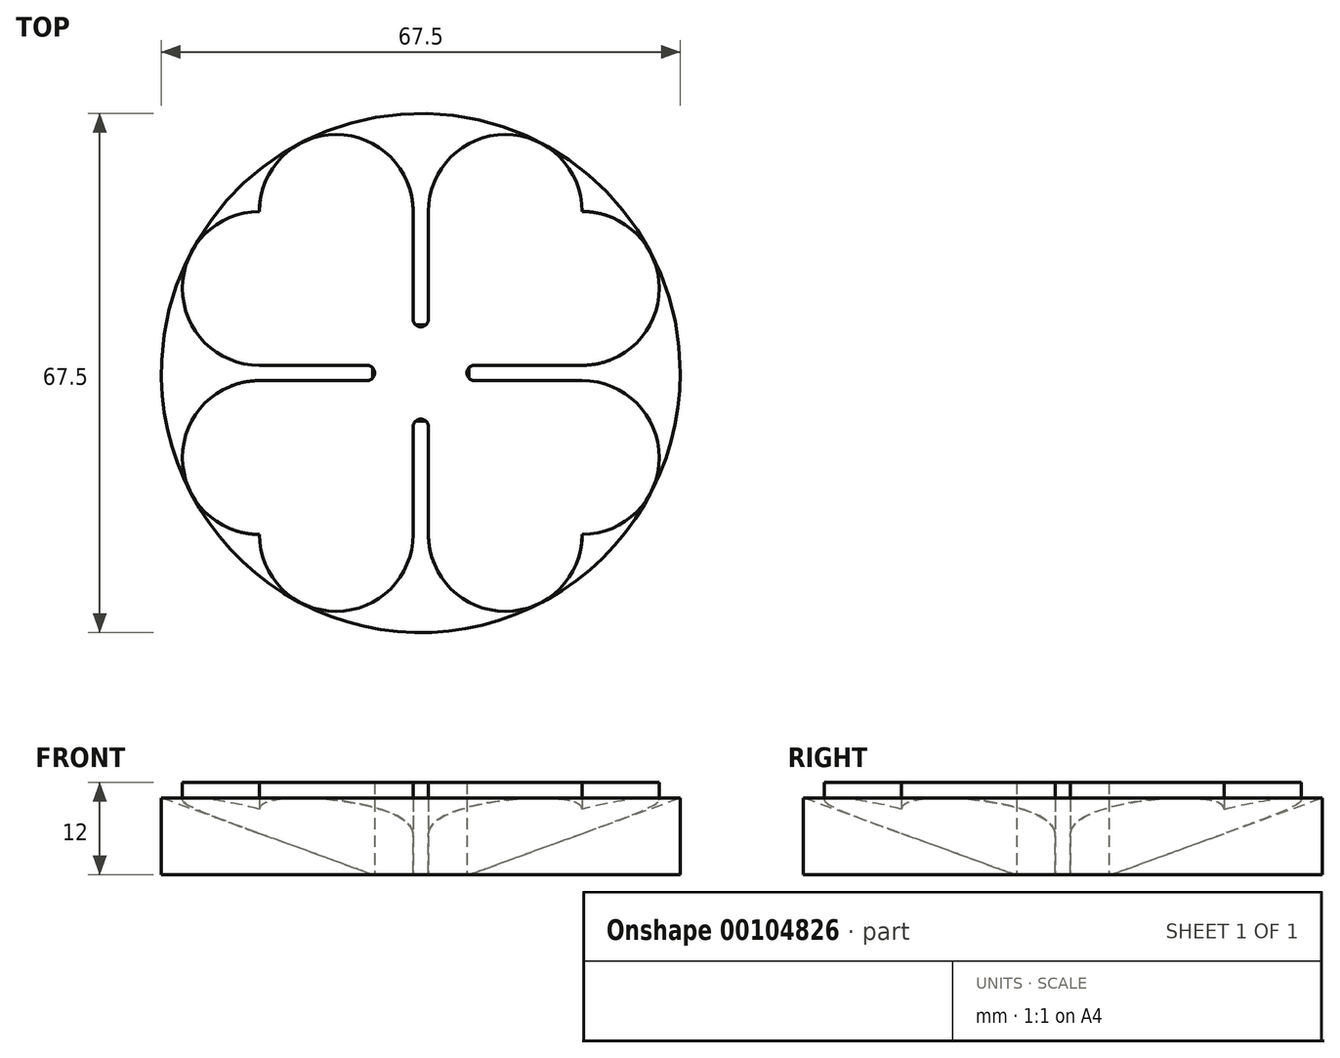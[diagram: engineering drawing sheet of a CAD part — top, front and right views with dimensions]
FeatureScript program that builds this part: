
annotation { "Feature Type Name" : "Feature", "Feature Type Description" : "" }
export const myFeature = defineFeature(function(context is Context, id is Id, definition is map)
    precondition{}
    {
        {
            var Q0;
            Q0=qCreatedBy(makeId("Top.planeOp"),FACE);
            var sketch = newSketch(context, id + "F0", { "sketchPlane" : qUnion([Q0])});
            skPoint(sketch, "E0.middle", {"position": v(0, 0) * mm});
            skLineSegment(sketch, "E1", {"start": v(0, 0) * mm, "end": v(-21, 0) * mm});
            skLineSegment(sketch, "E2", {"start": v(-21, 0) * mm, "end": v(-21, 11) * mm});
            skLineSegment(sketch, "E3", {"start": v(-21, 0) * mm, "end": v(-21, -11) * mm});
            skLineSegment(sketch, "E4", {"start": v(0, 0) * mm, "end": v(21, 0) * mm});
            skLineSegment(sketch, "E5", {"start": v(21, 0) * mm, "end": v(21, 11) * mm});
            skLineSegment(sketch, "E6", {"start": v(21, 0) * mm, "end": v(21, -11) * mm});
            skLineSegment(sketch, "E7", {"start": v(0, 0) * mm, "end": v(0, -21) * mm});
            skLineSegment(sketch, "E8", {"start": v(0, -21) * mm, "end": v(-11, -21) * mm});
            skLineSegment(sketch, "E9", {"start": v(0, -21) * mm, "end": v(11, -21) * mm});
            skCircle(sketch, "E10", {"center": v(11, -21) * mm, "radius": 10 * mm});
            skCircle(sketch, "E11", {"center": v(21, -11) * mm, "radius": 10 * mm});
            skCircle(sketch, "E12", {"center": v(21, 11) * mm, "radius": 10 * mm});
            skCircle(sketch, "E13", {"center": v(-21, 11) * mm, "radius": 10 * mm});
            skCircle(sketch, "E14", {"center": v(-21, -11) * mm, "radius": 10 * mm});
            skCircle(sketch, "E15", {"center": v(-11, -21) * mm, "radius": 10 * mm});
            skLineSegment(sketch, "E16", {"start": v(0, 0) * mm, "end": v(7, 0) * mm});
            skLineSegment(sketch, "E17", {"start": v(0, 0) * mm, "end": v(-7, 0) * mm});
            skLineSegment(sketch, "E18", {"start": v(0, 0) * mm, "end": v(0, -7) * mm});
            skCircle(sketch, "E19", {"center": v(7, 0) * mm, "radius": 1 * mm});
            skCircle(sketch, "E20", {"center": v(-7, 0) * mm, "radius": 1 * mm});
            skCircle(sketch, "E21", {"center": v(0, -7) * mm, "radius": 1 * mm});
            skLineSegment(sketch, "E22", {"start": v(0, 0) * mm, "end": v(0, 21) * mm});
            skLineSegment(sketch, "E23", {"start": v(0, 21) * mm, "end": v(11, 21) * mm});
            skLineSegment(sketch, "E24", {"start": v(0, 21) * mm, "end": v(-11, 21) * mm});
            skLineSegment(sketch, "E25", {"start": v(0, 0) * mm, "end": v(0, 7) * mm});
            skCircle(sketch, "E26", {"center": v(0, 7) * mm, "radius": 1 * mm});
            skCircle(sketch, "E27", {"center": v(-11, 21) * mm, "radius": 10 * mm});
            skCircle(sketch, "E28", {"center": v(11, 21) * mm, "radius": 10 * mm});
            skLineSegment(sketch, "E29", {"start": v(-1, 7) * mm, "end": v(-1, 21) * mm});
            skPoint(sketch, "E29.endSnap0", {"position": v(-5.5, 21) * mm});
            skLineSegment(sketch, "E30", {"start": v(7, 1) * mm, "end": v(21, 1) * mm});
            skLineSegment(sketch, "E31", {"start": v(7, -1) * mm, "end": v(21, -1) * mm});
            skLineSegment(sketch, "E32", {"start": v(1, -7) * mm, "end": v(1, -21) * mm});
            skLineSegment(sketch, "E33", {"start": v(-1, -7) * mm, "end": v(-1, -21) * mm});
            skLineSegment(sketch, "E34", {"start": v(-7, 1) * mm, "end": v(-21, 1) * mm});
            skLineSegment(sketch, "E35", {"start": v(-7, -1) * mm, "end": v(-21, -1) * mm});
            skCircle(sketch, "E36", {"center": v(0, 0) * mm, "radius": 33.75 * mm});
            skLineSegment(sketch, "E37", {"start": v(1, 7) * mm, "end": v(1, 21) * mm});
            skSolve(sketch);
        }
        {
            var Q0;
            {var subQ0=sQuery(id+"F0.wireOp",EDGE,"E13");var subQ2=sQuery(id+"F0.wireOp",EDGE,"E27");var subQ3=makeQuery(id+"F0.imprint","INTERSECT",VERTEX,{"disambiguationData":[OD(0.0)],"derivedFrom":[subQ0,subQ2]});Q0=makeQuery(id+"F0.imprint","IMPRINT",FACE,{"disambiguationData":[TD([[makeQuery(id+"F0.imprint","IMPRINT",EDGE,{"disambiguationData":[TD([[subQ3,-1.0]])],"derivedFrom":subQ2}),-1.0]])]});}
            var Q1;
            {var subQ0=sQuery(id+"F0.wireOp",EDGE,"E27");var subQ1=sQuery(id+"F0.wireOp",EDGE,"E13");var subQ2=makeQuery(id+"F0.imprint","INTERSECT",VERTEX,{"disambiguationData":[OD(0.0)],"derivedFrom":[subQ1,subQ0]});Q1=makeQuery(id+"F0.imprint","IMPRINT",FACE,{"disambiguationData":[TD([[makeQuery(id+"F0.imprint","IMPRINT",EDGE,{"disambiguationData":[TD([[subQ2,1.0]])],"derivedFrom":subQ1}),1.0]])]});}
            var Q2;
            {var subQ0=sQuery(id+"F0.wireOp",EDGE,"E27");var subQ1=sQuery(id+"F0.wireOp",EDGE,"E13");var subQ2=makeQuery(id+"F0.imprint","INTERSECT",VERTEX,{"disambiguationData":[OD(0.0)],"derivedFrom":[subQ1,subQ0]});Q2=makeQuery(id+"F0.imprint","IMPRINT",FACE,{"disambiguationData":[TD([[makeQuery(id+"F0.imprint","IMPRINT",EDGE,{"disambiguationData":[TD([[subQ2,1.0]])],"derivedFrom":subQ1}),-1.0]])]});}
            var Q3;
            {var subQ0=sQuery(id+"F0.wireOp",EDGE,"E28");var subQ1=sQuery(id+"F0.wireOp",EDGE,"E12");var subQ2=makeQuery(id+"F0.imprint","INTERSECT",VERTEX,{"disambiguationData":[OD(0.0)],"derivedFrom":[subQ1,subQ0]});Q3=makeQuery(id+"F0.imprint","IMPRINT",FACE,{"disambiguationData":[TD([[makeQuery(id+"F0.imprint","IMPRINT",EDGE,{"disambiguationData":[TD([[subQ2,1.0]])],"derivedFrom":subQ1}),-1.0]])]});}
            var Q4;
            {var subQ0=sQuery(id+"F0.wireOp",EDGE,"E28");var subQ1=sQuery(id+"F0.wireOp",EDGE,"E12");var subQ2=makeQuery(id+"F0.imprint","INTERSECT",VERTEX,{"disambiguationData":[OD(0.0)],"derivedFrom":[subQ1,subQ0]});Q4=makeQuery(id+"F0.imprint","IMPRINT",FACE,{"disambiguationData":[TD([[makeQuery(id+"F0.imprint","IMPRINT",EDGE,{"disambiguationData":[TD([[subQ2,1.0]])],"derivedFrom":subQ1}),1.0]])]});}
            var Q5;
            {var subQ0=sQuery(id+"F0.wireOp",EDGE,"E12");var subQ2=sQuery(id+"F0.wireOp",EDGE,"E28");var subQ3=makeQuery(id+"F0.imprint","INTERSECT",VERTEX,{"disambiguationData":[OD(0.0)],"derivedFrom":[subQ0,subQ2]});Q5=makeQuery(id+"F0.imprint","IMPRINT",FACE,{"disambiguationData":[TD([[makeQuery(id+"F0.imprint","IMPRINT",EDGE,{"disambiguationData":[TD([[subQ3,-1.0]])],"derivedFrom":subQ2}),-1.0]])]});}
            var Q6;
            {var subQ0=sQuery(id+"F0.wireOp",EDGE,"E11");var subQ1=sQuery(id+"F0.wireOp",EDGE,"E10");var subQ2=makeQuery(id+"F0.imprint","INTERSECT",VERTEX,{"disambiguationData":[OD(0.0)],"derivedFrom":[subQ1,subQ0]});Q6=makeQuery(id+"F0.imprint","IMPRINT",FACE,{"disambiguationData":[TD([[makeQuery(id+"F0.imprint","IMPRINT",EDGE,{"disambiguationData":[TD([[subQ2,1.0]])],"derivedFrom":subQ1}),-1.0]])]});}
            var Q7;
            {var subQ0=sQuery(id+"F0.wireOp",EDGE,"E11");var subQ1=sQuery(id+"F0.wireOp",EDGE,"E10");var subQ2=makeQuery(id+"F0.imprint","INTERSECT",VERTEX,{"disambiguationData":[OD(0.0)],"derivedFrom":[subQ1,subQ0]});Q7=makeQuery(id+"F0.imprint","IMPRINT",FACE,{"disambiguationData":[TD([[makeQuery(id+"F0.imprint","IMPRINT",EDGE,{"disambiguationData":[TD([[subQ2,1.0]])],"derivedFrom":subQ1}),1.0]])]});}
            var Q8;
            {var subQ0=sQuery(id+"F0.wireOp",EDGE,"E10");var subQ2=sQuery(id+"F0.wireOp",EDGE,"E11");var subQ3=makeQuery(id+"F0.imprint","INTERSECT",VERTEX,{"disambiguationData":[OD(0.0)],"derivedFrom":[subQ0,subQ2]});Q8=makeQuery(id+"F0.imprint","IMPRINT",FACE,{"disambiguationData":[TD([[makeQuery(id+"F0.imprint","IMPRINT",EDGE,{"disambiguationData":[TD([[subQ3,-1.0]])],"derivedFrom":subQ2}),-1.0]])]});}
            var Q9;
            {var subQ0=sQuery(id+"F0.wireOp",EDGE,"E15");var subQ1=sQuery(id+"F0.wireOp",EDGE,"E14");var subQ2=makeQuery(id+"F0.imprint","INTERSECT",VERTEX,{"disambiguationData":[OD(0.0)],"derivedFrom":[subQ1,subQ0]});Q9=makeQuery(id+"F0.imprint","IMPRINT",FACE,{"disambiguationData":[TD([[makeQuery(id+"F0.imprint","IMPRINT",EDGE,{"disambiguationData":[TD([[subQ2,1.0]])],"derivedFrom":subQ1}),-1.0]])]});}
            var Q10;
            {var subQ0=sQuery(id+"F0.wireOp",EDGE,"E15");var subQ1=sQuery(id+"F0.wireOp",EDGE,"E14");var subQ2=makeQuery(id+"F0.imprint","INTERSECT",VERTEX,{"disambiguationData":[OD(0.0)],"derivedFrom":[subQ1,subQ0]});Q10=makeQuery(id+"F0.imprint","IMPRINT",FACE,{"disambiguationData":[TD([[makeQuery(id+"F0.imprint","IMPRINT",EDGE,{"disambiguationData":[TD([[subQ2,1.0]])],"derivedFrom":subQ1}),1.0]])]});}
            var Q11;
            {var subQ0=sQuery(id+"F0.wireOp",EDGE,"E14");var subQ2=sQuery(id+"F0.wireOp",EDGE,"E15");var subQ3=makeQuery(id+"F0.imprint","INTERSECT",VERTEX,{"disambiguationData":[OD(0.0)],"derivedFrom":[subQ0,subQ2]});Q11=makeQuery(id+"F0.imprint","IMPRINT",FACE,{"disambiguationData":[TD([[makeQuery(id+"F0.imprint","IMPRINT",EDGE,{"disambiguationData":[TD([[subQ3,-1.0]])],"derivedFrom":subQ2}),-1.0]])]});}
            var Q12;
            {var subQ7=sQuery(id+"F0.wireOp",EDGE,"E33");Q12=makeQuery(id+"F0.imprint","IMPRINT",FACE,{"disambiguationData":[TD([[makeQuery(id+"F0.imprint","IMPRINT",EDGE,{"derivedFrom":subQ7}),-1.0]])]});}
            var Q13;
            {var subQ7=sQuery(id+"F0.wireOp",EDGE,"E31");Q13=makeQuery(id+"F0.imprint","IMPRINT",FACE,{"disambiguationData":[TD([[makeQuery(id+"F0.imprint","IMPRINT",EDGE,{"derivedFrom":subQ7}),-1.0]])]});}
            var Q14;
            {var subQ7=sQuery(id+"F0.wireOp",EDGE,"E30");Q14=makeQuery(id+"F0.imprint","IMPRINT",FACE,{"disambiguationData":[TD([[makeQuery(id+"F0.imprint","IMPRINT",EDGE,{"derivedFrom":subQ7}),1.0]])]});}
            var Q15;
            {var subQ11=sQuery(id+"F0.wireOp",EDGE,"E29");Q15=makeQuery(id+"F0.imprint","IMPRINT",FACE,{"disambiguationData":[TD([[makeQuery(id+"F0.imprint","IMPRINT",EDGE,{"derivedFrom":subQ11}),1.0]])]});}
            var Q16;
            Q16=makeQuery(id+"F0.imprint","IMPRINT",FACE,{"disambiguationData":[TD([[makeQuery(id+"F0.imprint","IMPRINT",EDGE,{"derivedFrom":sQuery(id+"F0.wireOp",EDGE,"E36")}),1.0]])]});
            var Q17;
            {var subQ5=sQuery(id+"F0.wireOp",EDGE,"E37");Q17=makeQuery(id+"F0.imprint","IMPRINT",FACE,{"disambiguationData":[TD([[makeQuery(id+"F0.imprint","IMPRINT",EDGE,{"derivedFrom":subQ5}),1.0]])]});}
            var Q18;
            {var subQ5=sQuery(id+"F0.wireOp",EDGE,"E29");Q18=makeQuery(id+"F0.imprint","IMPRINT",FACE,{"disambiguationData":[TD([[makeQuery(id+"F0.imprint","IMPRINT",EDGE,{"derivedFrom":subQ5}),-1.0]])]});}
            var Q19;
            {var subQ0=sQuery(id+"F0.wireOp",EDGE,"E25");var subQ1=sQuery(id+"F0.wireOp",EDGE,"E22");var subQ2=makeQuery(id+"F0.imprint","INTERSECT",VERTEX,{"derivedFrom":[subQ1,subQ0]});Q19=makeQuery(id+"F0.imprint","IMPRINT",FACE,{"disambiguationData":[TD([[makeQuery(id+"F0.imprint","IMPRINT",EDGE,{"disambiguationData":[TD([[subQ2,-1.0]])],"derivedFrom":subQ1}),1.0]])]});}
            var Q20;
            {var subQ0=sQuery(id+"F0.wireOp",EDGE,"E25");var subQ1=sQuery(id+"F0.wireOp",EDGE,"E22");var subQ2=makeQuery(id+"F0.imprint","INTERSECT",VERTEX,{"derivedFrom":[subQ1,subQ0]});Q20=makeQuery(id+"F0.imprint","IMPRINT",FACE,{"disambiguationData":[TD([[makeQuery(id+"F0.imprint","IMPRINT",EDGE,{"disambiguationData":[TD([[subQ2,-1.0]])],"derivedFrom":subQ1}),-1.0]])]});}
            var Q21;
            {var subQ5=sQuery(id+"F0.wireOp",EDGE,"E35");Q21=makeQuery(id+"F0.imprint","IMPRINT",FACE,{"disambiguationData":[TD([[makeQuery(id+"F0.imprint","IMPRINT",EDGE,{"derivedFrom":subQ5}),-1.0]])]});}
            var Q22;
            {var subQ5=sQuery(id+"F0.wireOp",EDGE,"E34");Q22=makeQuery(id+"F0.imprint","IMPRINT",FACE,{"disambiguationData":[TD([[makeQuery(id+"F0.imprint","IMPRINT",EDGE,{"derivedFrom":subQ5}),1.0]])]});}
            var Q23;
            {var subQ0=sQuery(id+"F0.wireOp",EDGE,"E17");var subQ1=sQuery(id+"F0.wireOp",EDGE,"E1");var subQ2=makeQuery(id+"F0.imprint","INTERSECT",VERTEX,{"derivedFrom":[subQ1,subQ0]});Q23=makeQuery(id+"F0.imprint","IMPRINT",FACE,{"disambiguationData":[TD([[makeQuery(id+"F0.imprint","IMPRINT",EDGE,{"disambiguationData":[TD([[subQ2,-1.0]])],"derivedFrom":subQ1}),-1.0]])]});}
            var Q24;
            {var subQ0=sQuery(id+"F0.wireOp",EDGE,"E17");var subQ1=sQuery(id+"F0.wireOp",EDGE,"E1");var subQ2=makeQuery(id+"F0.imprint","INTERSECT",VERTEX,{"derivedFrom":[subQ1,subQ0]});Q24=makeQuery(id+"F0.imprint","IMPRINT",FACE,{"disambiguationData":[TD([[makeQuery(id+"F0.imprint","IMPRINT",EDGE,{"disambiguationData":[TD([[subQ2,-1.0]])],"derivedFrom":subQ1}),1.0]])]});}
            var Q25;
            {var subQ0=sQuery(id+"F0.wireOp",EDGE,"E16");var subQ1=sQuery(id+"F0.wireOp",EDGE,"E4");var subQ2=makeQuery(id+"F0.imprint","INTERSECT",VERTEX,{"derivedFrom":[subQ1,subQ0]});Q25=makeQuery(id+"F0.imprint","IMPRINT",FACE,{"disambiguationData":[TD([[makeQuery(id+"F0.imprint","IMPRINT",EDGE,{"disambiguationData":[TD([[subQ2,-1.0]])],"derivedFrom":subQ1}),-1.0]])]});}
            var Q26;
            {var subQ0=sQuery(id+"F0.wireOp",EDGE,"E16");var subQ1=sQuery(id+"F0.wireOp",EDGE,"E4");var subQ2=makeQuery(id+"F0.imprint","INTERSECT",VERTEX,{"derivedFrom":[subQ1,subQ0]});Q26=makeQuery(id+"F0.imprint","IMPRINT",FACE,{"disambiguationData":[TD([[makeQuery(id+"F0.imprint","IMPRINT",EDGE,{"disambiguationData":[TD([[subQ2,-1.0]])],"derivedFrom":subQ1}),1.0]])]});}
            var Q27;
            {var subQ5=sQuery(id+"F0.wireOp",EDGE,"E30");Q27=makeQuery(id+"F0.imprint","IMPRINT",FACE,{"disambiguationData":[TD([[makeQuery(id+"F0.imprint","IMPRINT",EDGE,{"derivedFrom":subQ5}),-1.0]])]});}
            var Q28;
            {var subQ5=sQuery(id+"F0.wireOp",EDGE,"E31");Q28=makeQuery(id+"F0.imprint","IMPRINT",FACE,{"disambiguationData":[TD([[makeQuery(id+"F0.imprint","IMPRINT",EDGE,{"derivedFrom":subQ5}),1.0]])]});}
            var Q29;
            {var subQ5=sQuery(id+"F0.wireOp",EDGE,"E32");Q29=makeQuery(id+"F0.imprint","IMPRINT",FACE,{"disambiguationData":[TD([[makeQuery(id+"F0.imprint","IMPRINT",EDGE,{"derivedFrom":subQ5}),-1.0]])]});}
            var Q30;
            {var subQ5=sQuery(id+"F0.wireOp",EDGE,"E33");Q30=makeQuery(id+"F0.imprint","IMPRINT",FACE,{"disambiguationData":[TD([[makeQuery(id+"F0.imprint","IMPRINT",EDGE,{"derivedFrom":subQ5}),1.0]])]});}
            var Q31;
            {var subQ0=sQuery(id+"F0.wireOp",EDGE,"E18");var subQ1=sQuery(id+"F0.wireOp",EDGE,"E7");var subQ2=makeQuery(id+"F0.imprint","INTERSECT",VERTEX,{"derivedFrom":[subQ1,subQ0]});Q31=makeQuery(id+"F0.imprint","IMPRINT",FACE,{"disambiguationData":[TD([[makeQuery(id+"F0.imprint","IMPRINT",EDGE,{"disambiguationData":[TD([[subQ2,-1.0]])],"derivedFrom":subQ1}),-1.0]])]});}
            var Q32;
            {var subQ0=sQuery(id+"F0.wireOp",EDGE,"E18");var subQ1=sQuery(id+"F0.wireOp",EDGE,"E7");var subQ2=makeQuery(id+"F0.imprint","INTERSECT",VERTEX,{"derivedFrom":[subQ1,subQ0]});Q32=makeQuery(id+"F0.imprint","IMPRINT",FACE,{"disambiguationData":[TD([[makeQuery(id+"F0.imprint","IMPRINT",EDGE,{"disambiguationData":[TD([[subQ2,-1.0]])],"derivedFrom":subQ1}),1.0]])]});}
            extrude(context, id + "F1", {"entities" : qUnion([Q0, Q1, Q2, Q3, Q4, Q5, Q6, Q7, Q8, Q9, Q10, Q11, Q12, Q13, Q14, Q15, Q16, Q17, Q18, Q19, Q20, Q21, Q22, Q23, Q24, Q25, Q26, Q27, Q28, Q29, Q30, Q31, Q32]), "depth" : 10 * mm});
        }
        {
            var Q0;
            Q0=makeQuery(id+"F1.opExtrude","CAP_FACE",FACE,{"disambiguationData":[OSD([sQuery(id+"F0.wireOp",EDGE,"E36")])],"isStart":false});
            var sketch = newSketch(context, id + "F2", { "sketchPlane" : qUnion([Q0])});
            skCircle(sketch, "E38", {"center": v(0, 0) * mm, "radius": 33.75 * mm});
            skSolve(sketch);
        }
        {
            var Q0;
            Q0 = qSketchRegion(id + "F2", true);
            extrude(context, id + "F3", {"entities" : qUnion([Q0]), "operationType" : NewBodyOperationType.REMOVE, "oppositeDirection" : true, "depth" : 10 * mm, "hasDraft" : true, "draftAngle" : 70 * degree, "draftPullDirection" : true});
        }
        {
            var Q0;
            {var subQ0=sQuery(id+"F0.wireOp",EDGE,"E10");var subQ2=sQuery(id+"F0.wireOp",EDGE,"E11");var subQ3=makeQuery(id+"F0.imprint","INTERSECT",VERTEX,{"disambiguationData":[OD(0.0)],"derivedFrom":[subQ0,subQ2]});Q0=makeQuery(id+"F0.imprint","IMPRINT",FACE,{"disambiguationData":[TD([[makeQuery(id+"F0.imprint","IMPRINT",EDGE,{"disambiguationData":[TD([[subQ3,-1.0]])],"derivedFrom":subQ2}),-1.0]])]});}
            var Q1;
            {var subQ0=sQuery(id+"F0.wireOp",EDGE,"E11");var subQ1=sQuery(id+"F0.wireOp",EDGE,"E10");var subQ2=makeQuery(id+"F0.imprint","INTERSECT",VERTEX,{"disambiguationData":[OD(0.0)],"derivedFrom":[subQ1,subQ0]});Q1=makeQuery(id+"F0.imprint","IMPRINT",FACE,{"disambiguationData":[TD([[makeQuery(id+"F0.imprint","IMPRINT",EDGE,{"disambiguationData":[TD([[subQ2,1.0]])],"derivedFrom":subQ1}),1.0]])]});}
            var Q2;
            {var subQ0=sQuery(id+"F0.wireOp",EDGE,"E11");var subQ1=sQuery(id+"F0.wireOp",EDGE,"E10");var subQ2=makeQuery(id+"F0.imprint","INTERSECT",VERTEX,{"disambiguationData":[OD(0.0)],"derivedFrom":[subQ1,subQ0]});Q2=makeQuery(id+"F0.imprint","IMPRINT",FACE,{"disambiguationData":[TD([[makeQuery(id+"F0.imprint","IMPRINT",EDGE,{"disambiguationData":[TD([[subQ2,1.0]])],"derivedFrom":subQ1}),-1.0]])]});}
            var Q3;
            {var subQ0=sQuery(id+"F0.wireOp",EDGE,"E12");var subQ2=sQuery(id+"F0.wireOp",EDGE,"E28");var subQ3=makeQuery(id+"F0.imprint","INTERSECT",VERTEX,{"disambiguationData":[OD(0.0)],"derivedFrom":[subQ0,subQ2]});Q3=makeQuery(id+"F0.imprint","IMPRINT",FACE,{"disambiguationData":[TD([[makeQuery(id+"F0.imprint","IMPRINT",EDGE,{"disambiguationData":[TD([[subQ3,-1.0]])],"derivedFrom":subQ2}),-1.0]])]});}
            var Q4;
            {var subQ0=sQuery(id+"F0.wireOp",EDGE,"E28");var subQ1=sQuery(id+"F0.wireOp",EDGE,"E12");var subQ2=makeQuery(id+"F0.imprint","INTERSECT",VERTEX,{"disambiguationData":[OD(0.0)],"derivedFrom":[subQ1,subQ0]});Q4=makeQuery(id+"F0.imprint","IMPRINT",FACE,{"disambiguationData":[TD([[makeQuery(id+"F0.imprint","IMPRINT",EDGE,{"disambiguationData":[TD([[subQ2,1.0]])],"derivedFrom":subQ1}),1.0]])]});}
            var Q5;
            {var subQ0=sQuery(id+"F0.wireOp",EDGE,"E28");var subQ1=sQuery(id+"F0.wireOp",EDGE,"E12");var subQ2=makeQuery(id+"F0.imprint","INTERSECT",VERTEX,{"disambiguationData":[OD(0.0)],"derivedFrom":[subQ1,subQ0]});Q5=makeQuery(id+"F0.imprint","IMPRINT",FACE,{"disambiguationData":[TD([[makeQuery(id+"F0.imprint","IMPRINT",EDGE,{"disambiguationData":[TD([[subQ2,1.0]])],"derivedFrom":subQ1}),-1.0]])]});}
            var Q6;
            {var subQ0=sQuery(id+"F0.wireOp",EDGE,"E27");var subQ1=sQuery(id+"F0.wireOp",EDGE,"E13");var subQ2=makeQuery(id+"F0.imprint","INTERSECT",VERTEX,{"disambiguationData":[OD(0.0)],"derivedFrom":[subQ1,subQ0]});Q6=makeQuery(id+"F0.imprint","IMPRINT",FACE,{"disambiguationData":[TD([[makeQuery(id+"F0.imprint","IMPRINT",EDGE,{"disambiguationData":[TD([[subQ2,1.0]])],"derivedFrom":subQ1}),-1.0]])]});}
            var Q7;
            {var subQ0=sQuery(id+"F0.wireOp",EDGE,"E27");var subQ1=sQuery(id+"F0.wireOp",EDGE,"E13");var subQ2=makeQuery(id+"F0.imprint","INTERSECT",VERTEX,{"disambiguationData":[OD(0.0)],"derivedFrom":[subQ1,subQ0]});Q7=makeQuery(id+"F0.imprint","IMPRINT",FACE,{"disambiguationData":[TD([[makeQuery(id+"F0.imprint","IMPRINT",EDGE,{"disambiguationData":[TD([[subQ2,1.0]])],"derivedFrom":subQ1}),1.0]])]});}
            var Q8;
            {var subQ0=sQuery(id+"F0.wireOp",EDGE,"E13");var subQ2=sQuery(id+"F0.wireOp",EDGE,"E27");var subQ3=makeQuery(id+"F0.imprint","INTERSECT",VERTEX,{"disambiguationData":[OD(0.0)],"derivedFrom":[subQ0,subQ2]});Q8=makeQuery(id+"F0.imprint","IMPRINT",FACE,{"disambiguationData":[TD([[makeQuery(id+"F0.imprint","IMPRINT",EDGE,{"disambiguationData":[TD([[subQ3,-1.0]])],"derivedFrom":subQ2}),-1.0]])]});}
            var Q9;
            {var subQ0=sQuery(id+"F0.wireOp",EDGE,"E14");var subQ2=sQuery(id+"F0.wireOp",EDGE,"E15");var subQ3=makeQuery(id+"F0.imprint","INTERSECT",VERTEX,{"disambiguationData":[OD(0.0)],"derivedFrom":[subQ0,subQ2]});Q9=makeQuery(id+"F0.imprint","IMPRINT",FACE,{"disambiguationData":[TD([[makeQuery(id+"F0.imprint","IMPRINT",EDGE,{"disambiguationData":[TD([[subQ3,-1.0]])],"derivedFrom":subQ2}),-1.0]])]});}
            var Q10;
            {var subQ0=sQuery(id+"F0.wireOp",EDGE,"E15");var subQ1=sQuery(id+"F0.wireOp",EDGE,"E14");var subQ2=makeQuery(id+"F0.imprint","INTERSECT",VERTEX,{"disambiguationData":[OD(0.0)],"derivedFrom":[subQ1,subQ0]});Q10=makeQuery(id+"F0.imprint","IMPRINT",FACE,{"disambiguationData":[TD([[makeQuery(id+"F0.imprint","IMPRINT",EDGE,{"disambiguationData":[TD([[subQ2,1.0]])],"derivedFrom":subQ1}),-1.0]])]});}
            var Q11;
            {var subQ0=sQuery(id+"F0.wireOp",EDGE,"E15");var subQ1=sQuery(id+"F0.wireOp",EDGE,"E14");var subQ2=makeQuery(id+"F0.imprint","INTERSECT",VERTEX,{"disambiguationData":[OD(0.0)],"derivedFrom":[subQ1,subQ0]});Q11=makeQuery(id+"F0.imprint","IMPRINT",FACE,{"disambiguationData":[TD([[makeQuery(id+"F0.imprint","IMPRINT",EDGE,{"disambiguationData":[TD([[subQ2,1.0]])],"derivedFrom":subQ1}),1.0]])]});}
            var Q12;
            {var subQ7=sQuery(id+"F0.wireOp",EDGE,"E33");Q12=makeQuery(id+"F0.imprint","IMPRINT",FACE,{"disambiguationData":[TD([[makeQuery(id+"F0.imprint","IMPRINT",EDGE,{"derivedFrom":subQ7}),-1.0]])]});}
            var Q13;
            {var subQ7=sQuery(id+"F0.wireOp",EDGE,"E31");Q13=makeQuery(id+"F0.imprint","IMPRINT",FACE,{"disambiguationData":[TD([[makeQuery(id+"F0.imprint","IMPRINT",EDGE,{"derivedFrom":subQ7}),-1.0]])]});}
            var Q14;
            {var subQ7=sQuery(id+"F0.wireOp",EDGE,"E30");Q14=makeQuery(id+"F0.imprint","IMPRINT",FACE,{"disambiguationData":[TD([[makeQuery(id+"F0.imprint","IMPRINT",EDGE,{"derivedFrom":subQ7}),1.0]])]});}
            var Q15;
            {var subQ11=sQuery(id+"F0.wireOp",EDGE,"E29");Q15=makeQuery(id+"F0.imprint","IMPRINT",FACE,{"disambiguationData":[TD([[makeQuery(id+"F0.imprint","IMPRINT",EDGE,{"derivedFrom":subQ11}),1.0]])]});}
            extrude(context, id + "F4", {"entities" : qUnion([Q0, Q1, Q2, Q3, Q4, Q5, Q6, Q7, Q8, Q9, Q10, Q11, Q12, Q13, Q14, Q15]), "operationType" : NewBodyOperationType.ADD, "depth" : 12 * mm});
        }
    });
